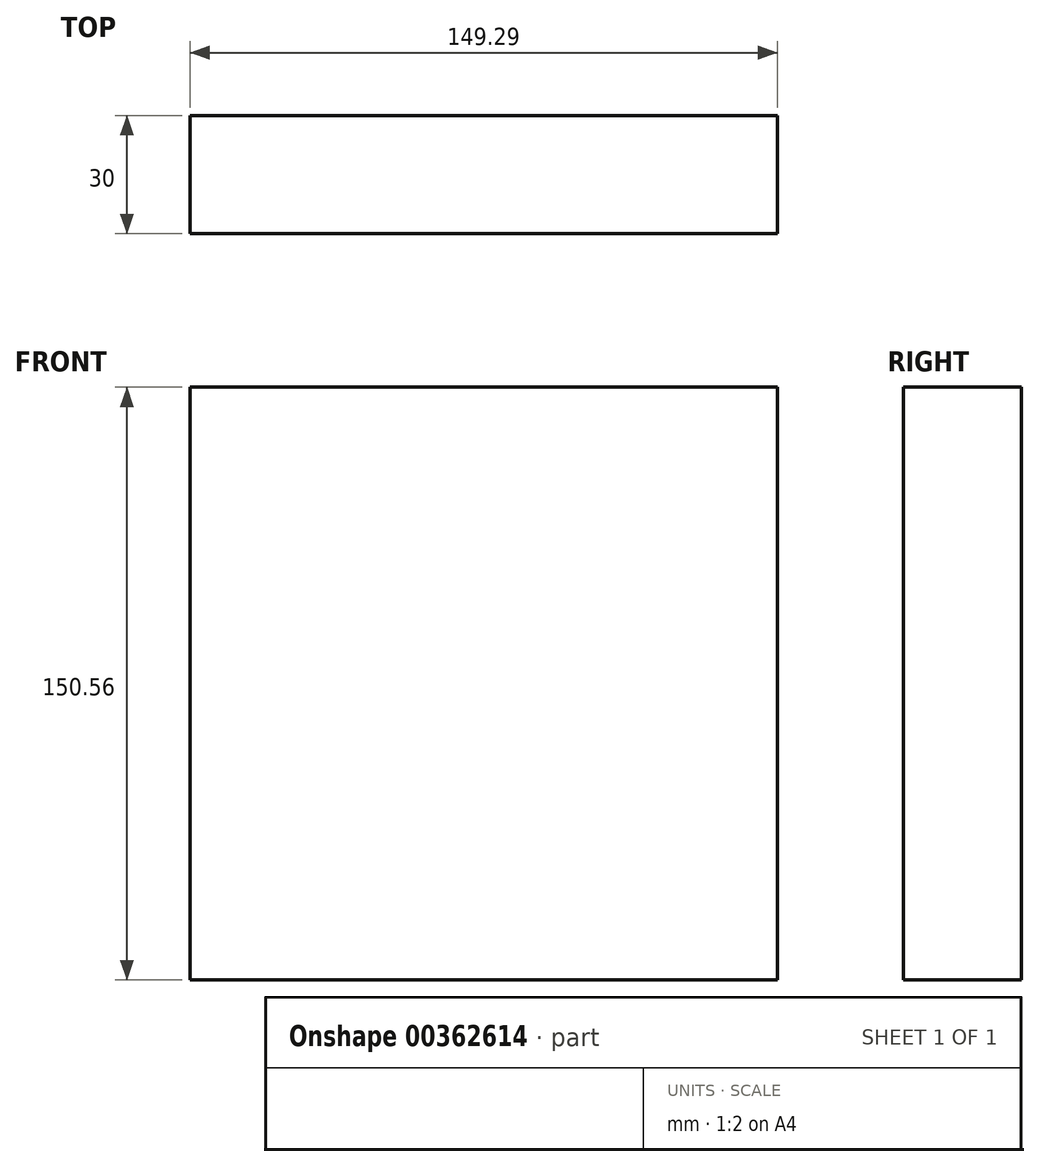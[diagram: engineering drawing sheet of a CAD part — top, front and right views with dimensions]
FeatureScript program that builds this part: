
annotation { "Feature Type Name" : "Feature", "Feature Type Description" : "" }
export const myFeature = defineFeature(function(context is Context, id is Id, definition is map)
    precondition{}
    {
        {
            var Q0;
            Q0=qCreatedBy(makeId("Front.planeOp"),FACE);
            var sketch = newSketch(context, id + "F0", { "sketchPlane" : qUnion([Q0])});
            skLineSegment(sketch, "E0.bottom", {"start": v(-74.75, 75.07) * mm, "end": v(74.54, 75.07) * mm});
            skLineSegment(sketch, "E0.top", {"start": v(-74.75, -75.5) * mm, "end": v(74.54, -75.5) * mm});
            skLineSegment(sketch, "E0.left", {"start": v(-74.75, 75.07) * mm, "end": v(-74.75, -75.5) * mm});
            skLineSegment(sketch, "E0.right", {"start": v(74.54, 75.07) * mm, "end": v(74.54, -75.5) * mm});
            skSolve(sketch);
        }
        {
            var Q0;
            Q0=makeQuery(id+"F0.imprint","IMPRINT",FACE,{"disambiguationData":[TD([[makeQuery(id+"F0.imprint","IMPRINT",EDGE,{"derivedFrom":sQuery(id+"F0.wireOp",EDGE,"E0.bottom")}),-1.0]])]});
            extrude(context, id + "F1", {"entities" : qUnion([Q0]), "oppositeDirection" : true, "depth" : 30 * mm, "offsetDistance" : 25 * mm});
        }
        {
            var Q0;
            Q0=makeQuery(id+"F0.imprint","IMPRINT",FACE,{"disambiguationData":[TD([[makeQuery(id+"F0.imprint","IMPRINT",EDGE,{"derivedFrom":sQuery(id+"F0.wireOp",EDGE,"E0.bottom")}),-1.0]])]});
            var sketch = newSketch(context, id + "F2", { "sketchPlane" : qUnion([Q0])});
            skCircle(sketch, "E1", {"center": v(0, 0) * mm, "radius": 48.17 * mm});
            skCircle(sketch, "E2", {"center": v(45.27, 16.46) * mm, "radius": 28.86 * mm});
            skCircle(sketch, "E3", {"center": v(16.57, 13.5) * mm, "radius": 14.56 * mm});
            skSolve(sketch);
        }
        {
            var Q0;
            Q0=sQuery(id+"F2.wireOp",EDGE,"E1");
            extrude(context, id + "F3", {"bodyType" : ToolBodyType.SURFACE, "surfaceEntities" : qUnion([Q0]), "depth" : 25 * mm, "offsetDistance" : 25 * mm});
        }
    });
